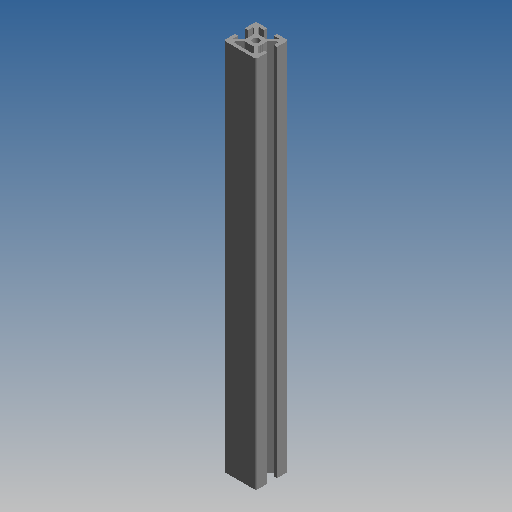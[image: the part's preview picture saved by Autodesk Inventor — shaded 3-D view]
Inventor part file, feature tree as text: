
AUTODESK INVENTOR PART (.ipt)
format: ipt  version: 2020 (Build 240168000, 168)  size: 203,264 bytes
history: native  units: mm (DEFAULTED — no unit token found)
features: other x7, sketch x2, extrude x1, hole x1
ambient origin geometry x8: Origin, YZ Plane, XZ Plane, XY Plane, X Axis, Y Axis, Z Axis, Center Point
bodies: Solid1 (feature_tree)
feature tree (11):
  extrude  "Extrusion1"  TaperAngle=0.0deg  [1 undecoded]
  hole  "Hole1"  [1 undecoded]
  other  "C1_XY"
  other  "C1_YZ"
  other  "C1_ZX"
  other  "C1_X"
  other  "C1_Y"
  other  "C1_Z"
  other  "C1_Center"
  sketch  "Sketch_76"  dims[d2=4.2mm d3=6.0mm d4=4.0mm d5=2.0mm d6=90.0deg d7=231.0mm d8=0.0mm d9=0.0mm]
  sketch  "Sketch2"  dims[d0=231.0mm d1=0.0mm]
note: 2 required parameter values undecoded (feature->parameter linkage not recoverable at this tier; creation-order binding heuristic only, values carry confidence <= 0.55)
